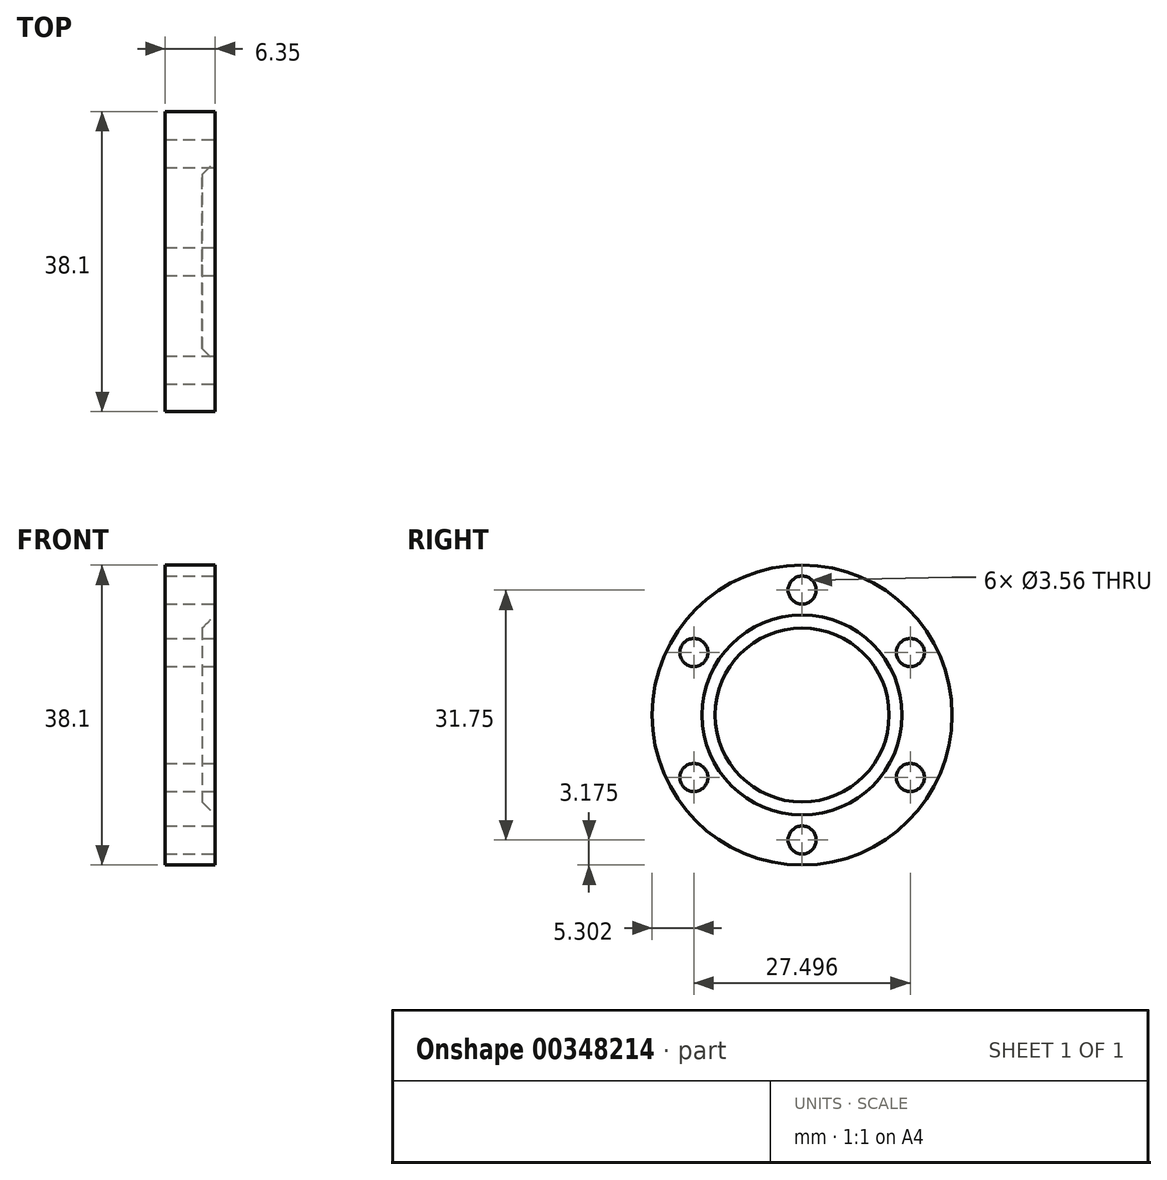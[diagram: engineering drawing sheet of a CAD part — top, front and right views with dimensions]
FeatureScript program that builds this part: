
annotation { "Feature Type Name" : "Feature", "Feature Type Description" : "" }
export const myFeature = defineFeature(function(context is Context, id is Id, definition is map)
    precondition{}
    {
        {
            var Q0;
            Q0=qCreatedBy(makeId("Front.planeOp"),FACE);
            var sketch = newSketch(context, id + "F0", { "sketchPlane" : qUnion([Q0])});
            skLineSegment(sketch, "E0", {"start": v(0, 12.7) * mm, "end": v(0, 19.05) * mm});
            skLineSegment(sketch, "E1", {"start": v(0, 19.05) * mm, "end": v(-6.35, 19.05) * mm});
            skLineSegment(sketch, "E2", {"start": v(-6.35, 19.05) * mm, "end": v(-6.35, 0) * mm});
            skLineSegment(sketch, "E3", {"start": v(-1.65, 11.05) * mm, "end": v(0, 12.7) * mm});
            skLineSegment(sketch, "E4", {"start": v(-6.35, 0) * mm, "end": v(-1.65, 0) * mm});
            skLineSegment(sketch, "E5", {"start": v(-1.65, 0) * mm, "end": v(-1.65, 11.05) * mm});
            skSolve(sketch);
        }
        {
            var Q0;
            Q0=qSketchRegion(id+"F0",true);
            var Q1;
            Q1=sQuery(id+"F0.wireOp",EDGE,"E4");
            revolve(context, id + "F1", {"entities" : qUnion([Q0]), "axis" : qUnion([Q1]), "revolveType" : RevolveType.FULL});
        }
        {
            var Q0;
            Q0=qCreatedBy(makeId("Right.planeOp"),FACE);
            var sketch = newSketch(context, id + "F2", { "sketchPlane" : qUnion([Q0])});
            skCircle(sketch, "E6", {"center": v(0, 15.88) * mm, "radius": 1.78 * mm});
            skCircle(sketch, "E7", {"center": v(0, 0) * mm, "radius": 15.88 * mm, "construction": true});
            skCircle(sketch, "E8.1.0", {"center": v(-13.75, 7.94) * mm, "radius": 1.78 * mm});
            skCircle(sketch, "E8.2.0", {"center": v(-13.75, -7.94) * mm, "radius": 1.78 * mm});
            skCircle(sketch, "E8.3.0", {"center": v(0, -15.88) * mm, "radius": 1.78 * mm});
            skCircle(sketch, "E8.4.0", {"center": v(13.75, -7.94) * mm, "radius": 1.78 * mm});
            skCircle(sketch, "E8.5.0", {"center": v(13.75, 7.94) * mm, "radius": 1.78 * mm});
            skSolve(sketch);
        }
        {
            var Q0;
            Q0=qSketchRegion(id+"F2",true);
            extrude(context, id + "F3", {"entities" : qUnion([Q0]), "operationType" : NewBodyOperationType.REMOVE, "endBound" : BoundingType.THROUGH_ALL, "oppositeDirection" : true, "depth" : 25.4 * mm});
        }
    });
